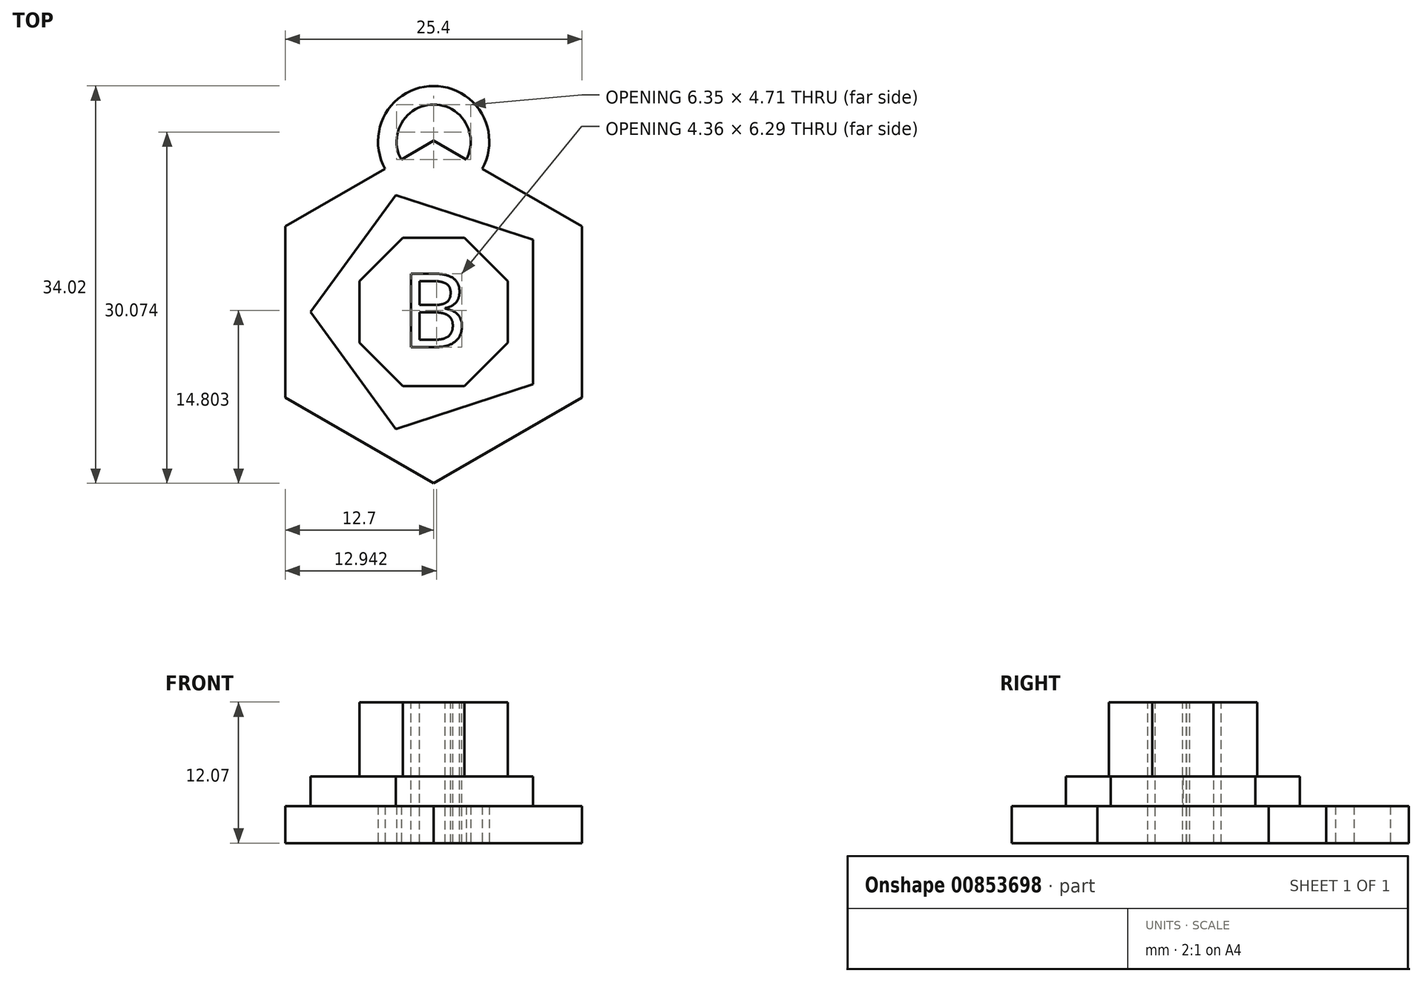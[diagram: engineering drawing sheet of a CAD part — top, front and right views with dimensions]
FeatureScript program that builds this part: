
annotation { "Feature Type Name" : "Feature", "Feature Type Description" : "" }
export const myFeature = defineFeature(function(context is Context, id is Id, definition is map)
    precondition{}
    {
        {
            var Q0;
            Q0=qCreatedBy(makeId("Top.planeOp"),FACE);
            var sketch = newSketch(context, id + "F0", { "sketchPlane" : qUnion([Q0])});
            skCircle(sketch, "E0.cCircle", {"center": v(0, 0) * mm, "radius": 12.7 * mm, "construction": true});
            skLineSegment(sketch, "E0.0", {"start": v(12.7, 7.33) * mm, "end": v(12.7, -7.33) * mm});
            skLineSegment(sketch, "E0.1", {"start": v(12.7, -7.33) * mm, "end": v(0, -14.66) * mm});
            skLineSegment(sketch, "E0.2", {"start": v(0, -14.66) * mm, "end": v(-12.7, -7.33) * mm});
            skLineSegment(sketch, "E0.3", {"start": v(-12.7, -7.33) * mm, "end": v(-12.7, 7.33) * mm});
            skLineSegment(sketch, "E0.4", {"start": v(-12.7, 7.33) * mm, "end": v(0, 14.66) * mm});
            skLineSegment(sketch, "E0.5", {"start": v(0, 14.66) * mm, "end": v(12.7, 7.33) * mm});
            skPoint(sketch, "E0.0.midPoint", {"position": v(12.7, 0) * mm});
            skSolve(sketch);
        }
        {
            var Q0;
            Q0=makeQuery(id+"F0.imprint","IMPRINT",FACE,{"disambiguationData":[TD([[makeQuery(id+"F0.imprint","IMPRINT",EDGE,{"derivedFrom":sQuery(id+"F0.wireOp",EDGE,"E0.0")}),-1.0]])]});
            extrude(context, id + "F1", {"entities" : qUnion([Q0]), "depth" : 3.17 * mm, "offsetDistance" : 25.4 * mm});
        }
        {
            var Q0;
            Q0=makeQuery(id+"F1.opExtrude","CAP_FACE",FACE,{"disambiguationData":[OSD([sQuery(id+"F0.wireOp",EDGE,"E0.0"),sQuery(id+"F0.wireOp",EDGE,"E0.1"),sQuery(id+"F0.wireOp",EDGE,"E0.2"),sQuery(id+"F0.wireOp",EDGE,"E0.3"),sQuery(id+"F0.wireOp",EDGE,"E0.4"),sQuery(id+"F0.wireOp",EDGE,"E0.5")])],"isStart":false});
            var sketch = newSketch(context, id + "F2", { "sketchPlane" : qUnion([Q0])});
            skCircle(sketch, "E1.cCircle", {"center": v(0, 0) * mm, "radius": 8.52 * mm, "construction": true});
            skLineSegment(sketch, "E1.0", {"start": v(8.52, 6.19) * mm, "end": v(8.52, -6.19) * mm});
            skLineSegment(sketch, "E1.1", {"start": v(8.52, -6.19) * mm, "end": v(-3.25, -10.02) * mm});
            skLineSegment(sketch, "E1.2", {"start": v(-3.25, -10.02) * mm, "end": v(-10.53, 0) * mm});
            skLineSegment(sketch, "E1.3", {"start": v(-10.53, 0) * mm, "end": v(-3.25, 10.02) * mm});
            skLineSegment(sketch, "E1.4", {"start": v(-3.25, 10.02) * mm, "end": v(8.52, 6.19) * mm});
            skPoint(sketch, "E1.0.midPoint", {"position": v(8.52, 0) * mm});
            skSolve(sketch);
        }
        {
            var Q0;
            Q0=makeQuery(id+"F2.imprint","IMPRINT",FACE,{"disambiguationData":[TD([[makeQuery(id+"F2.imprint","IMPRINT",EDGE,{"derivedFrom":sQuery(id+"F2.wireOp",EDGE,"E1.0")}),-1.0]])]});
            extrude(context, id + "F3", {"entities" : qUnion([Q0]), "operationType" : NewBodyOperationType.ADD, "depth" : 2.54 * mm, "offsetDistance" : 25.4 * mm});
        }
        {
            var Q0;
            Q0=makeQuery(id+"F3.opExtrude","CAP_FACE",FACE,{"disambiguationData":[OSD([sQuery(id+"F2.wireOp",EDGE,"E1.0"),sQuery(id+"F2.wireOp",EDGE,"E1.1"),sQuery(id+"F2.wireOp",EDGE,"E1.2"),sQuery(id+"F2.wireOp",EDGE,"E1.3"),sQuery(id+"F2.wireOp",EDGE,"E1.4")])],"isStart":false});
            var sketch = newSketch(context, id + "F4", { "sketchPlane" : qUnion([Q0])});
            skCircle(sketch, "E2.cCircle", {"center": v(0, 0) * mm, "radius": 6.35 * mm, "construction": true});
            skLineSegment(sketch, "E2.0", {"start": v(6.35, 2.63) * mm, "end": v(6.35, -2.63) * mm});
            skLineSegment(sketch, "E2.1", {"start": v(6.35, -2.63) * mm, "end": v(2.63, -6.35) * mm});
            skLineSegment(sketch, "E2.2", {"start": v(2.63, -6.35) * mm, "end": v(-2.63, -6.35) * mm});
            skLineSegment(sketch, "E2.3", {"start": v(-2.63, -6.35) * mm, "end": v(-6.35, -2.63) * mm});
            skLineSegment(sketch, "E2.4", {"start": v(-6.35, -2.63) * mm, "end": v(-6.35, 2.63) * mm});
            skLineSegment(sketch, "E2.5", {"start": v(-6.35, 2.63) * mm, "end": v(-2.63, 6.35) * mm});
            skLineSegment(sketch, "E2.6", {"start": v(-2.63, 6.35) * mm, "end": v(2.63, 6.35) * mm});
            skLineSegment(sketch, "E2.7", {"start": v(2.63, 6.35) * mm, "end": v(6.35, 2.63) * mm});
            skPoint(sketch, "E2.0.midPoint", {"position": v(6.35, 0) * mm});
            skSolve(sketch);
        }
        {
            var Q0;
            Q0=makeQuery(id+"F4.imprint","IMPRINT",FACE,{"disambiguationData":[TD([[makeQuery(id+"F4.imprint","IMPRINT",EDGE,{"derivedFrom":sQuery(id+"F4.wireOp",EDGE,"E2.0")}),-1.0]])]});
            extrude(context, id + "F5", {"entities" : qUnion([Q0]), "operationType" : NewBodyOperationType.ADD, "depth" : 6.35 * mm, "offsetDistance" : 25.4 * mm});
        }
        {
            var Q0;
            Q0=makeQuery(id+"F5.opExtrude","CAP_FACE",FACE,{"disambiguationData":[OSD([sQuery(id+"F4.wireOp",EDGE,"E2.0"),sQuery(id+"F4.wireOp",EDGE,"E2.1"),sQuery(id+"F4.wireOp",EDGE,"E2.2"),sQuery(id+"F4.wireOp",EDGE,"E2.3"),sQuery(id+"F4.wireOp",EDGE,"E2.4"),sQuery(id+"F4.wireOp",EDGE,"E2.5"),sQuery(id+"F4.wireOp",EDGE,"E2.6"),sQuery(id+"F4.wireOp",EDGE,"E2.7")])],"isStart":false});
            var sketch = newSketch(context, id + "F6", { "sketchPlane" : qUnion([Q0])});
            skText(sketch, "E3", { "text": "B", "fontName": "OpenSans-Regular.ttf"});
            const initialGuessF6  = {"E3": [-0.0028, -0.003, 1, 0, 0.00634]};
            skSetInitialGuess(sketch, initialGuessF6);
            skSolve(sketch);
        }
        {
            var Q0;
            Q0=makeQuery(id+"F6.imprint","IMPRINT",FACE,{"disambiguationData":[TD([[makeQuery(id+"F6.imprint","IMPRINT",EDGE,{"derivedFrom":sQuery(id+"F6.wireOp",EDGE,"E3.sketch_text.stroke-0")}),-1.0]])]});
            extrude(context, id + "F7", {"entities" : qUnion([Q0]), "operationType" : NewBodyOperationType.REMOVE, "oppositeDirection" : true, "depth" : 12.7 * mm, "offsetDistance" : 25.4 * mm});
        }
        {
            var Q0;
            Q0=qCreatedBy(makeId("Top.planeOp"),FACE);
            var sketch = newSketch(context, id + "F8", { "sketchPlane" : qUnion([Q0])});
            skCircle(sketch, "E4", {"center": v(0, 14.6) * mm, "radius": 4.76 * mm});
            skCircle(sketch, "E5", {"center": v(0, 14.6) * mm, "radius": 3.18 * mm});
            skSolve(sketch);
        }
        {
            var Q0;
            Q0=makeQuery(id+"F8.imprint","IMPRINT",FACE,{"disambiguationData":[TD([[makeQuery(id+"F8.imprint","IMPRINT",EDGE,{"derivedFrom":sQuery(id+"F8.wireOp",EDGE,"E4")}),1.0]])]});
            var Q1;
            Q1=makeQuery(id+"F1.opExtrude","CAP_FACE",FACE,{"disambiguationData":[OSD([sQuery(id+"F0.wireOp",EDGE,"E0.0"),sQuery(id+"F0.wireOp",EDGE,"E0.1"),sQuery(id+"F0.wireOp",EDGE,"E0.2"),sQuery(id+"F0.wireOp",EDGE,"E0.3"),sQuery(id+"F0.wireOp",EDGE,"E0.4"),sQuery(id+"F0.wireOp",EDGE,"E0.5")])],"isStart":false});
            extrude(context, id + "F9", {"entities" : qUnion([Q0]), "operationType" : NewBodyOperationType.ADD, "endBound" : BoundingType.UP_TO_SURFACE, "depth" : 25.4 * mm, "endBoundEntityFace" : qUnion([Q1]), "offsetDistance" : 25.4 * mm});
        }
    });
